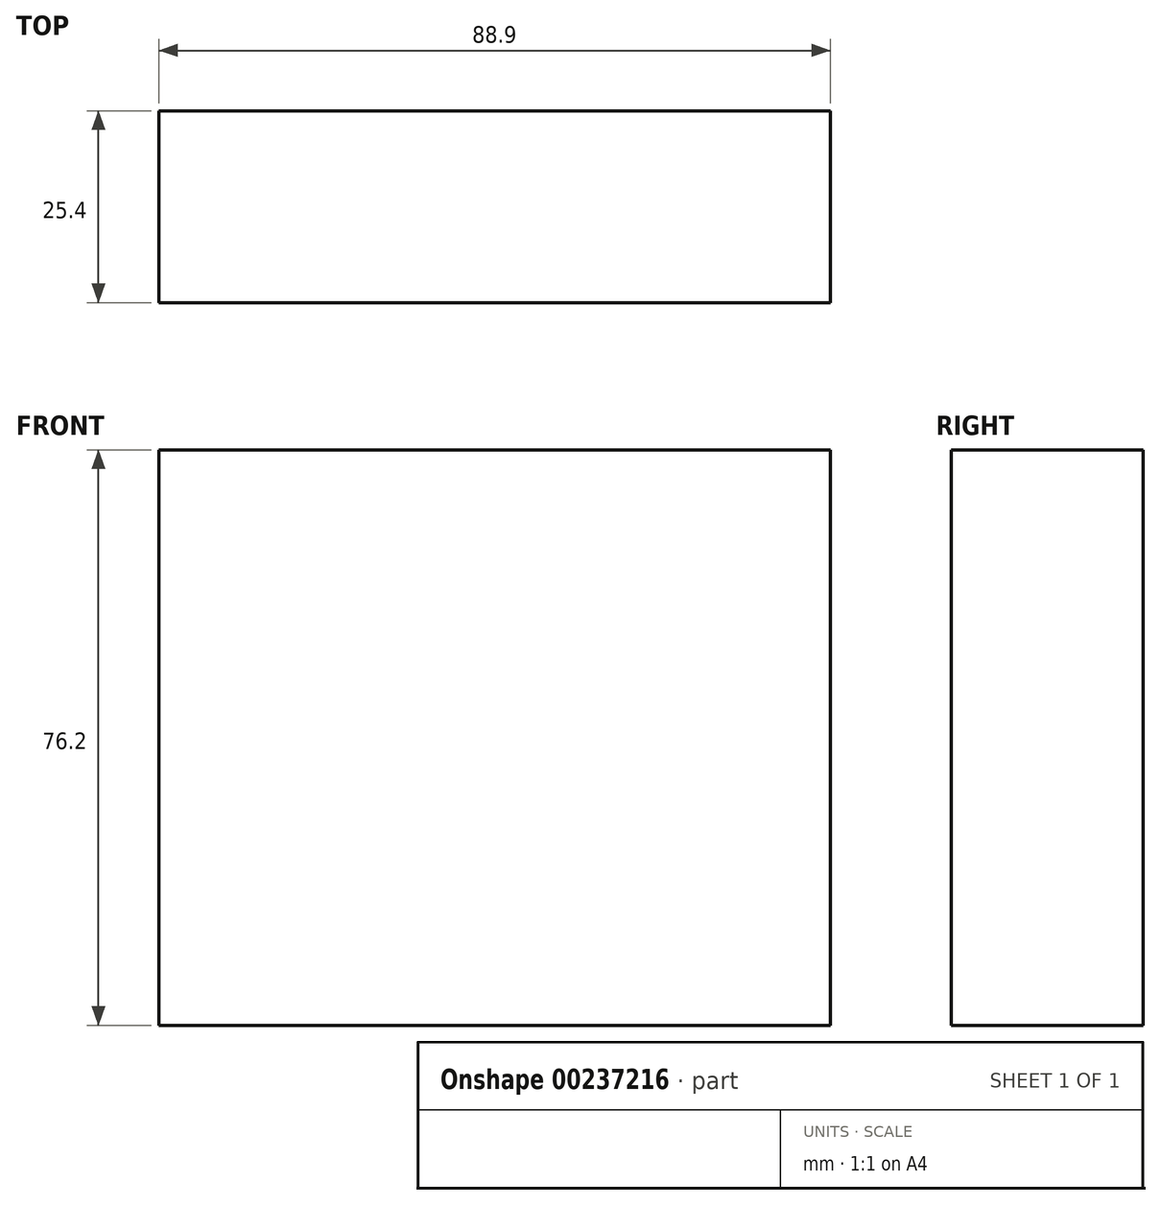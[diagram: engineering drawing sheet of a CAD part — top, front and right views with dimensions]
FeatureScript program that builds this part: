
annotation { "Feature Type Name" : "Feature", "Feature Type Description" : "" }
export const myFeature = defineFeature(function(context is Context, id is Id, definition is map)
    precondition{}
    {
        {
            var Q0;
            Q0=qCreatedBy(makeId("Top.planeOp"),FACE);
            var sketch = newSketch(context, id + "F0", { "sketchPlane" : qUnion([Q0])});
            skLineSegment(sketch, "E0.bottom", {"start": v(0, 0) * mm, "end": v(88.9, 0) * mm});
            skLineSegment(sketch, "E0.top", {"start": v(0, 25.4) * mm, "end": v(88.9, 25.4) * mm});
            skLineSegment(sketch, "E0.left", {"start": v(0, 0) * mm, "end": v(0, 25.4) * mm});
            skLineSegment(sketch, "E0.right", {"start": v(88.9, 0) * mm, "end": v(88.9, 25.4) * mm});
            skSolve(sketch);
        }
        {
            var Q0;
            Q0=makeQuery(id+"F0.imprint","IMPRINT",FACE,{"disambiguationData":[TD([[makeQuery(id+"F0.imprint","IMPRINT",EDGE,{"derivedFrom":sQuery(id+"F0.wireOp",EDGE,"E0.bottom")}),1.0]])]});
            extrude(context, id + "F1", {"entities" : qUnion([Q0]), "depth" : 76.2 * mm});
        }
    });
